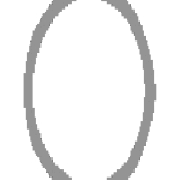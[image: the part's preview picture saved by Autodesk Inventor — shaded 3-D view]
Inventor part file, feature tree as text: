
AUTODESK INVENTOR PART (.ipt)
format: ipt  version: 2021 (Build 250183000, 183)  size: 110,080 bytes
history: native  units: in
note: dims shown in document units (in); Inventor stores cm internally (conversion verified against a paired STEP export)
features: other x4, sketch x3, plane x1
ambient origin geometry x8: Origin, YZ Plane, XZ Plane, XY Plane, X Axis, Y Axis, Z Axis, Center Point
bodies: Solid1 (feature_tree), Body (feature_tree)
feature tree (8):
  other  "Driven Length"
  other  "Frame Generator"
  other  "Start Plane"
  other  "End Plane"
  sketch  "Sketch"  dims[d2=13.5in d4=-0.0in d5=13.5in d6=0.12in d7=0.0in d10=90.0deg d9=13.5in]
  sketch  "Sketch4"  dims[d0=1.0in]
  plane  "Work Plane4"
  sketch  "Sketch5"  dims[d1=0.065in]
